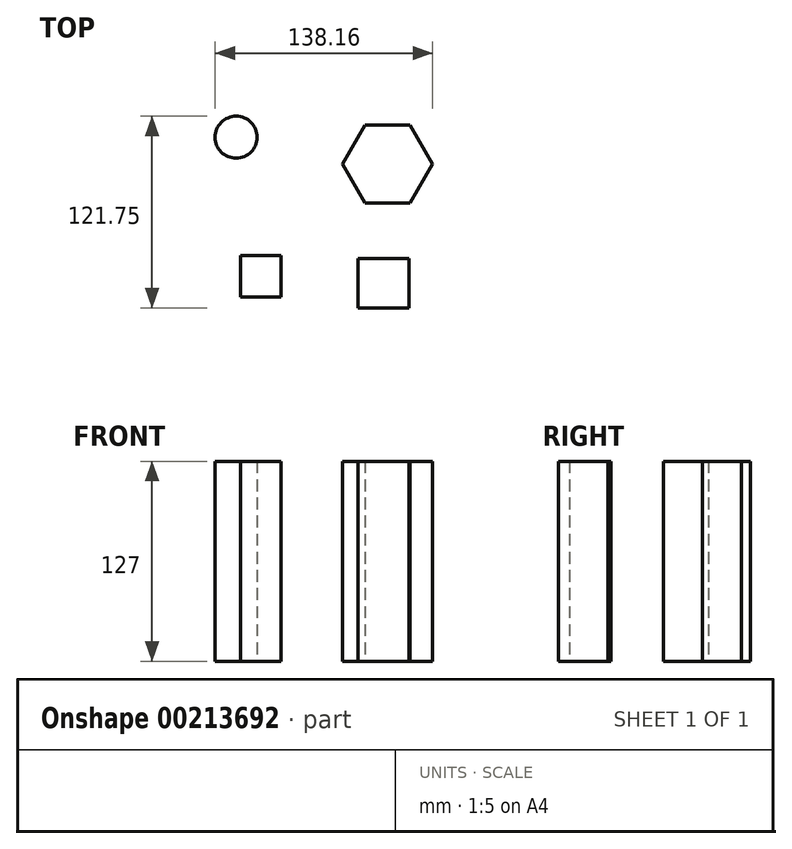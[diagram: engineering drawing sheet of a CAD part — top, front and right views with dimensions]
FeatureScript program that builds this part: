
annotation { "Feature Type Name" : "Feature", "Feature Type Description" : "" }
export const myFeature = defineFeature(function(context is Context, id is Id, definition is map)
    precondition{}
    {
        {
            var Q0;
            Q0=qCreatedBy(makeId("Top.planeOp"),FACE);
            var sketch = newSketch(context, id + "F0", { "sketchPlane" : qUnion([Q0])});
            skCircle(sketch, "E0", {"center": v(-60.3, 54.11) * mm, "radius": 13.34 * mm});
            skLineSegment(sketch, "E1.bottom", {"start": v(49.4, -22.85) * mm, "end": v(17.2, -22.85) * mm});
            skLineSegment(sketch, "E1.top", {"start": v(49.4, -54.3) * mm, "end": v(17.2, -54.3) * mm});
            skLineSegment(sketch, "E1.left", {"start": v(49.4, -22.85) * mm, "end": v(49.4, -54.3) * mm});
            skLineSegment(sketch, "E1.right", {"start": v(17.2, -22.85) * mm, "end": v(17.2, -54.3) * mm});
            skPoint(sketch, "E1.middle", {"position": v(33.3, -38.57) * mm});
            skLineSegment(sketch, "E2.bottom", {"start": v(-57.35, -47.27) * mm, "end": v(-31.82, -47.27) * mm});
            skLineSegment(sketch, "E2.top", {"start": v(-57.35, -21) * mm, "end": v(-31.82, -21) * mm});
            skLineSegment(sketch, "E2.left", {"start": v(-57.35, -47.27) * mm, "end": v(-57.35, -21) * mm});
            skLineSegment(sketch, "E2.right", {"start": v(-31.82, -47.27) * mm, "end": v(-31.82, -21) * mm});
            skCircle(sketch, "E3.cCircle", {"center": v(35.89, 37.1) * mm, "radius": 24.79 * mm, "construction": true});
            skLineSegment(sketch, "E3.0", {"start": v(21.58, 61.88) * mm, "end": v(50.2, 61.88) * mm});
            skLineSegment(sketch, "E3.1", {"start": v(50.2, 61.88) * mm, "end": v(64.51, 37.1) * mm});
            skLineSegment(sketch, "E3.2", {"start": v(64.51, 37.1) * mm, "end": v(50.2, 12.3) * mm});
            skLineSegment(sketch, "E3.3", {"start": v(50.2, 12.3) * mm, "end": v(21.58, 12.3) * mm});
            skLineSegment(sketch, "E3.4", {"start": v(21.58, 12.3) * mm, "end": v(7.26, 37.1) * mm});
            skLineSegment(sketch, "E3.5", {"start": v(7.26, 37.1) * mm, "end": v(21.58, 61.88) * mm});
            skPoint(sketch, "E3.0.midPoint", {"position": v(35.89, 61.88) * mm});
            skSolve(sketch);
        }
        {
            var Q0;
            Q0 = qSketchRegion(id + "F0", true);
            extrude(context, id + "F1", {"entities" : qUnion([Q0]), "depth" : 127 * mm});
        }
    });
